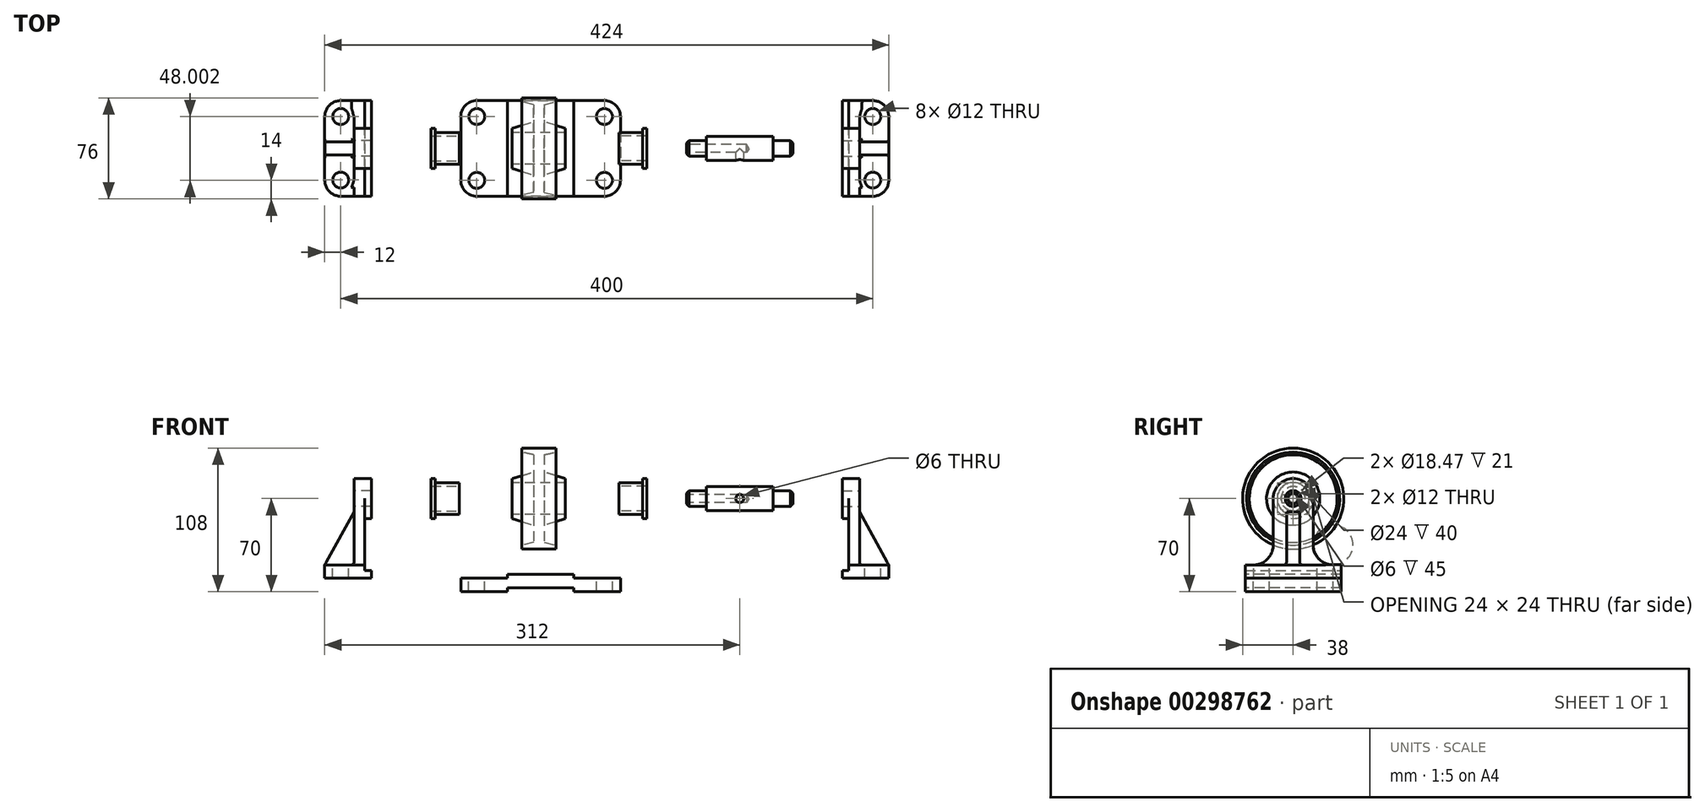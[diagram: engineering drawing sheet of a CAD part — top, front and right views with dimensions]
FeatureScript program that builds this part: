
annotation { "Feature Type Name" : "Feature", "Feature Type Description" : "" }
export const myFeature = defineFeature(function(context is Context, id is Id, definition is map)
    precondition{}
    {
        {
            var Q0;
            Q0=qCreatedBy(makeId("Front.planeOp"),FACE);
            var sketch = newSketch(context, id + "F0", { "sketchPlane" : qUnion([Q0])});
            skLineSegment(sketch, "E0", {"start": v(-300.95, 0) * mm, "end": v(299.05, 0) * mm});
            skSolve(sketch);
        }
        {
            var Q0;
            Q0=qCreatedBy(makeId("Front.planeOp"),FACE);
            var sketch = newSketch(context, id + "F1", { "sketchPlane" : qUnion([Q0])});
            skLineSegment(sketch, "E1", {"start": v(0, 12) * mm, "end": v(20, 12) * mm});
            skLineSegment(sketch, "E2", {"start": v(20, 12) * mm, "end": v(20, 15) * mm});
            skLineSegment(sketch, "E3", {"start": v(20, 15) * mm, "end": v(4, 20) * mm});
            skLineSegment(sketch, "E4", {"start": v(4, 20) * mm, "end": v(4, 33) * mm});
            skLineSegment(sketch, "E5", {"start": v(4, 33) * mm, "end": v(13, 35) * mm});
            skLineSegment(sketch, "E6", {"start": v(13, 35) * mm, "end": v(13, 38) * mm});
            skLineSegment(sketch, "E7", {"start": v(13, 38) * mm, "end": v(0, 38) * mm});
            skLineSegment(sketch, "E8.MirrorCS", {"start": v(-13, 35) * mm, "end": v(-13, 38) * mm});
            skLineSegment(sketch, "E9.MirrorCS", {"start": v(-20, 12) * mm, "end": v(-20, 15) * mm});
            skLineSegment(sketch, "E10.MirrorCS", {"start": v(-13, 38) * mm, "end": v(0, 38) * mm});
            skLineSegment(sketch, "E11.MirrorCS", {"start": v(-4, 33) * mm, "end": v(-13, 35) * mm});
            skLineSegment(sketch, "E12.MirrorCS", {"start": v(-4, 20) * mm, "end": v(-4, 33) * mm});
            skLineSegment(sketch, "E13.MirrorCS", {"start": v(-20, 15) * mm, "end": v(-4, 20) * mm});
            skLineSegment(sketch, "E14.MirrorCS", {"start": v(0, 12) * mm, "end": v(-20, 12) * mm});
            skSolve(sketch);
        }
        {
            var Q0;
            Q0 = qSketchRegion(id + "F1", true);
            var Q1;
            Q1=sQuery(id+"F0.wireOp",EDGE,"E0");
            revolve(context, id + "F2", {"entities" : qUnion([Q0]), "axis" : qUnion([Q1]), "revolveType" : RevolveType.FULL});
        }
        {
            var Q0;
            Q0=qCreatedBy(makeId("Right.planeOp"),FACE);
            cPlane(context, id + "F3", {"entities" : qUnion([Q0]), "cplaneType" : CPlaneType.OFFSET, "offset" : 60 * mm, "oppositeDirection" : true, "width" : 150 * mm, "height" : 150 * mm});
        }
        {
            var Q0;
            Q0=qCreatedBy(id+"F3.planeOp",FACE);
            var sketch = newSketch(context, id + "F4", { "sketchPlane" : qUnion([Q0])});
            skCircle(sketch, "E15.0", {"center": v(0, 0) * mm, "radius": 12 * mm});
            skCircle(sketch, "E16", {"center": v(0, 0) * mm, "radius": 9.24 * mm});
            skSolve(sketch);
        }
        {
            var Q0;
            Q0 = qSketchRegion(id + "F4", true);
            extrude(context, id + "F5", {"entities" : qUnion([Q0]), "oppositeDirection" : true, "depth" : 21 * mm});
        }
        {
            var Q0;
            Q0=makeQuery(id+"F5.opExtrude","CAP_FACE",FACE,{"disambiguationData":[OSD([sQuery(id+"F4.wireOp",EDGE,"E15.0"),sQuery(id+"F4.wireOp",EDGE,"E16")])],"isStart":false});
            var sketch = newSketch(context, id + "F6", { "sketchPlane" : qUnion([Q0])});
            skCircle(sketch, "E17.0", {"center": v(0, 0) * mm, "radius": 9.24 * mm});
            skCircle(sketch, "E18", {"center": v(0, 0) * mm, "radius": 15 * mm});
            skSolve(sketch);
        }
        {
            var Q0;
            Q0 = qSketchRegion(id + "F6", true);
            extrude(context, id + "F7", {"entities" : qUnion([Q0]), "operationType" : NewBodyOperationType.ADD, "oppositeDirection" : true, "depth" : 3 * mm});
        }
        {
            var Q0;
            Q0=makeQuery(id+"F5.opExtrude","SWEPT_BODY",BODY,{"disambiguationData":[OSD([sQuery(id+"F4.wireOp",EDGE,"E15.0"),sQuery(id+"F4.wireOp",EDGE,"E16")])]});
            var Q1;
            Q1=qCreatedBy(makeId("Right.planeOp"),FACE);
            mirror(context, id + "F8", {"entities" : qUnion([Q0]), "mirrorPlane" : qUnion([Q1])});
        }
        {
            var Q0;
            Q0=makeQuery(id+"F8.opPattern","COPY",FACE,{"derivedFrom":makeQuery(id+"F7.boolean.opBoolean","MERGE",FACE,{"derivedFrom":[makeQuery(id+"F5.opExtrude","CAP_FACE",FACE,{"disambiguationData":[OSD([sQuery(id+"F4.wireOp",EDGE,"E15.0"),sQuery(id+"F4.wireOp",EDGE,"E16")])],"isStart":false}),makeQuery(id+"F7.opExtrude","CAP_FACE",FACE,{"disambiguationData":[OSD([sQuery(id+"F6.wireOp",EDGE,"E17.0"),sQuery(id+"F6.wireOp",EDGE,"E18")])],"isStart":true})]}),"instanceName":"1"});
            cPlane(context, id + "F9", {"entities" : qUnion([Q0]), "cplaneType" : CPlaneType.OFFSET, "offset" : 60 * mm, "width" : 150 * mm, "height" : 150 * mm});
        }
        {
            var Q0;
            Q0=qCreatedBy(id+"F9.planeOp",FACE);
            var sketch = newSketch(context, id + "F10", { "sketchPlane" : qUnion([Q0])});
            skCircle(sketch, "E19", {"center": v(0, 0) * mm, "radius": 6 * mm});
            skLineSegment(sketch, "E20", {"start": v(0, 10.72) * mm, "end": v(0, -9.05) * mm, "construction": true});
            skLineSegment(sketch, "E21", {"start": v(11.8, 0) * mm, "end": v(-12.55, 0) * mm, "construction": true});
            skSolve(sketch);
        }
        {
            var Q0;
            Q0 = qSketchRegion(id + "F10", true);
            extrude(context, id + "F11", {"entities" : qUnion([Q0]), "depth" : 80 * mm});
        }
        {
            var Q0;
            Q0=makeQuery(id+"F11.opExtrude","SWEPT_FACE",FACE,{"disambiguationData":[OSD([sQuery(id+"F10.wireOp",EDGE,"E19")])]});
            var Q1;
            Q1=makeQuery(id+"F11.opExtrude","CAP_FACE",FACE,{"disambiguationData":[OSD([sQuery(id+"F10.wireOp",EDGE,"E19")])],"isStart":true});
            chamfer(context, id + "F12", {"entities" : qUnion([Q0, Q1]), "width" : 2 * mm, "tangentPropagation" : true});
        }
        {
            var Q0;
            Q0=qCreatedBy(id+"F9.planeOp",FACE);
            cPlane(context, id + "F13", {"entities" : qUnion([Q0]), "cplaneType" : CPlaneType.OFFSET, "offset" : 15 * mm, "width" : 150 * mm, "height" : 150 * mm});
        }
        {
            var Q0;
            Q0=qCreatedBy(id+"F13.planeOp",FACE);
            var sketch = newSketch(context, id + "F14", { "sketchPlane" : qUnion([Q0])});
            skCircle(sketch, "E22", {"center": v(0, 0) * mm, "radius": 9 * mm});
            skSolve(sketch);
        }
        {
            var Q0;
            Q0 = qSketchRegion(id + "F14", true);
            extrude(context, id + "F15", {"entities" : qUnion([Q0]), "operationType" : NewBodyOperationType.ADD, "depth" : 50 * mm});
        }
        {
            var Q0;
            Q0=makeQuery(id+"F11.opExtrude","SWEPT_BODY",BODY,{"disambiguationData":[OSD([sQuery(id+"F10.wireOp",EDGE,"E19")])]});
            transform(context, id + "F16", {"entities" : qUnion([Q0]), "transformType" : TransformType.TRANSLATION_3D, "dx" : -20 * mm, "dy" : 0 * mm, "dz" : 0 * mm, "makeCopy" : false});
        }
        {
            var Q0;
            Q0=makeQuery(id+"F11.opExtrude","SWEPT_BODY",BODY,{"disambiguationData":[OSD([sQuery(id+"F10.wireOp",EDGE,"E19")])]});
            transform(context, id + "F17", {"entities" : qUnion([Q0]), "transformType" : TransformType.TRANSLATION_3D, "dx" : -10 * mm, "dy" : 0 * mm, "dz" : 0 * mm, "makeCopy" : false});
        }
        {
            var Q0;
            Q0=makeQuery(id+"F11.opExtrude","CAP_FACE",FACE,{"disambiguationData":[OSD([sQuery(id+"F10.wireOp",EDGE,"E19")])],"isStart":true});
            var sketch = newSketch(context, id + "F18", { "sketchPlane" : qUnion([Q0])});
            skCircle(sketch, "E23.0", {"center": v(0, 0) * mm, "radius": 4 * mm});
            skSolve(sketch);
        }
        {
            var Q0;
            Q0=sQuery(id+"F18.wireOp",VERTEX,"E23.0.center");
            var Q1;
            Q1=makeQuery(id+"F11.opExtrude","SWEPT_BODY",BODY,{"disambiguationData":[OSD([sQuery(id+"F10.wireOp",EDGE,"E19")])]});
            hole(context, id + "F19", {"style" : HoleStyle.SIMPLE, "endStyle" : HoleEndStyle.BLIND, "holeDiameter" : 6 * mm, "holeDepth" : 45 * mm, "tappedDepth" : 12 * mm, "tapClearance" : 3, "startFromSketch" : true, "locations" : qUnion([Q0]), "scope" : qUnion([Q1])});
        }
        {
            var Q0;
            Q0=qCreatedBy(makeId("Front.planeOp"),FACE);
            var sketch = newSketch(context, id + "F20", { "sketchPlane" : qUnion([Q0])});
            skCircle(sketch, "E24", {"center": v(151, 0) * mm, "radius": 3 * mm});
            skSolve(sketch);
        }
        {
            var Q0;
            Q0 = qSketchRegion(id + "F20", true);
            extrude(context, id + "F21", {"entities" : qUnion([Q0]), "operationType" : NewBodyOperationType.REMOVE, "depth" : 25 * mm});
        }
        {
            var Q0;
            Q0=makeQuery(id+"F7.boolean.opBoolean","MERGE",FACE,{"derivedFrom":[makeQuery(id+"F5.opExtrude","CAP_FACE",FACE,{"disambiguationData":[OSD([sQuery(id+"F4.wireOp",EDGE,"E15.0"),sQuery(id+"F4.wireOp",EDGE,"E16")])],"isStart":false}),makeQuery(id+"F7.opExtrude","CAP_FACE",FACE,{"disambiguationData":[OSD([sQuery(id+"F6.wireOp",EDGE,"E17.0"),sQuery(id+"F6.wireOp",EDGE,"E18")])],"isStart":true})]});
            cPlane(context, id + "F22", {"entities" : qUnion([Q0]), "cplaneType" : CPlaneType.OFFSET, "offset" : 100 * mm, "width" : 150 * mm, "height" : 150 * mm});
        }
        {
            var Q0;
            Q0=qCreatedBy(id+"F22.planeOp",FACE);
            var sketch = newSketch(context, id + "F23", { "sketchPlane" : qUnion([Q0])});
            skCircle(sketch, "E25.0", {"center": v(0, 0) * mm, "radius": 6 * mm});
            skCircle(sketch, "E26", {"center": v(0, 0) * mm, "radius": 15 * mm});
            skLineSegment(sketch, "E27", {"start": v(-15, 0) * mm, "end": v(-15, -49.82) * mm});
            skLineSegment(sketch, "E28", {"start": v(-15, -49.82) * mm, "end": v(-36, -49.82) * mm});
            skLineSegment(sketch, "E29", {"start": v(15, 0) * mm, "end": v(15, -50) * mm});
            skLineSegment(sketch, "E30", {"start": v(15, -50) * mm, "end": v(36, -50) * mm});
            skLineSegment(sketch, "E31", {"start": v(36, -50) * mm, "end": v(36, -60) * mm});
            skLineSegment(sketch, "E32", {"start": v(36, -60) * mm, "end": v(-36, -60) * mm});
            skLineSegment(sketch, "E33", {"start": v(-36, -60) * mm, "end": v(-36, -49.82) * mm});
            skSolve(sketch);
        }
        {
            var Q0;
            Q0=makeQuery(id+"F23.imprint","IMPRINT",FACE,{"disambiguationData":[TD([[makeQuery(id+"F23.imprint","IMPRINT",EDGE,{"derivedFrom":sQuery(id+"F23.wireOp",EDGE,"E25.0")}),-1.0]])]});
            extrude(context, id + "F24", {"entities" : qUnion([Q0]), "oppositeDirection" : true, "depth" : 5 * mm});
        }
        {
            var Q0;
            Q0=qCreatedBy(id+"F22.planeOp",FACE);
            var sketch = newSketch(context, id + "F25", { "sketchPlane" : qUnion([Q0])});
            skCircle(sketch, "E34.0", {"center": v(0, 0) * mm, "radius": 15 * mm});
            skCircle(sketch, "E35.0", {"center": v(0, 0) * mm, "radius": 6 * mm});
            skLineSegment(sketch, "E36.0", {"start": v(-15, 0) * mm, "end": v(-15, -49.82) * mm});
            skLineSegment(sketch, "E37.0", {"start": v(-15, -49.82) * mm, "end": v(-36, -49.82) * mm});
            skLineSegment(sketch, "E38.0", {"start": v(15, 0) * mm, "end": v(15, -50) * mm});
            skLineSegment(sketch, "E39.0", {"start": v(15, -50) * mm, "end": v(36, -50) * mm});
            skPoint(sketch, "E40.0", {"position": v(36, -55) * mm});
            skLineSegment(sketch, "E41.0", {"start": v(36, -50) * mm, "end": v(36, -60) * mm});
            skLineSegment(sketch, "E42.0", {"start": v(36, -60) * mm, "end": v(-36, -60) * mm});
            skLineSegment(sketch, "E43.0", {"start": v(-36, -60) * mm, "end": v(-36, -49.82) * mm});
            skSolve(sketch);
        }
        {
            var Q0;
            Q0 = qSketchRegion(id + "F25", true);
            extrude(context, id + "F26", {"entities" : qUnion([Q0]), "operationType" : NewBodyOperationType.ADD, "depth" : 8 * mm});
        }
        {
            var Q0;
            Q0=qCreatedBy(id+"F22.planeOp",FACE);
            var sketch = newSketch(context, id + "F27", { "sketchPlane" : qUnion([Q0])});
            skLineSegment(sketch, "E44.0", {"start": v(36, -60) * mm, "end": v(-36, -60) * mm});
            skLineSegment(sketch, "E45", {"start": v(36, -60) * mm, "end": v(36, -54) * mm});
            skLineSegment(sketch, "E46", {"start": v(36, -54) * mm, "end": v(-36, -54) * mm});
            skLineSegment(sketch, "E47", {"start": v(-36, -54) * mm, "end": v(-36, -60) * mm});
            skSolve(sketch);
        }
        {
            var Q0;
            Q0 = qSketchRegion(id + "F27", true);
            extrude(context, id + "F28", {"entities" : qUnion([Q0]), "operationType" : NewBodyOperationType.ADD, "oppositeDirection" : true, "depth" : 5 * mm});
        }
        {
            var Q0;
            Q0=makeQuery(id+"F26.opExtrude","CAP_FACE",FACE,{"disambiguationData":[OSD([sQuery(id+"F25.wireOp",EDGE,"E34.0"),sQuery(id+"F25.wireOp",EDGE,"E35.0"),sQuery(id+"F25.wireOp",EDGE,"E36.0"),sQuery(id+"F25.wireOp",EDGE,"E37.0"),sQuery(id+"F25.wireOp",EDGE,"E38.0"),sQuery(id+"F25.wireOp",EDGE,"E39.0"),sQuery(id+"F25.wireOp",EDGE,"E41.0"),sQuery(id+"F25.wireOp",EDGE,"E42.0"),sQuery(id+"F25.wireOp",EDGE,"E43.0")])],"isStart":false});
            var sketch = newSketch(context, id + "F29", { "sketchPlane" : qUnion([Q0])});
            skLineSegment(sketch, "E48.0", {"start": v(36, -60) * mm, "end": v(-36, -60) * mm});
            skLineSegment(sketch, "E49", {"start": v(-36, -60) * mm, "end": v(-36, -49.82) * mm});
            skLineSegment(sketch, "E50", {"start": v(-36, -49.82) * mm, "end": v(36, -50) * mm});
            skLineSegment(sketch, "E51", {"start": v(36, -50) * mm, "end": v(36, -60) * mm});
            skSolve(sketch);
        }
        {
            var Q0;
            Q0 = qSketchRegion(id + "F29", true);
            extrude(context, id + "F30", {"entities" : qUnion([Q0]), "operationType" : NewBodyOperationType.ADD, "depth" : 22 * mm});
        }
        {
            var Q0;
            Q0=makeQuery(id+"F26.opExtrude","SWEPT_EDGE",EDGE,{"disambiguationData":[OSD([sQuery(id+"F25.wireOp",EDGE,"E38.0"),sQuery(id+"F25.wireOp",EDGE,"E39.0")])]});
            var Q1;
            Q1=makeQuery(id+"F26.opExtrude","SWEPT_EDGE",EDGE,{"disambiguationData":[OSD([sQuery(id+"F25.wireOp",EDGE,"E36.0"),sQuery(id+"F25.wireOp",EDGE,"E37.0")])]});
            fillet(context, id + "F31", {"entities" : qUnion([Q0, Q1]), "radius" : 15 * mm, "tangentPropagation" : true, "allowEdgeOverflow" : false});
        }
        {
            var Q0;
            Q0=makeQuery(id+"F30.opExtrude","CAP_EDGE",EDGE,{"disambiguationData":[OSD([sQuery(id+"F29.wireOp",EDGE,"E51")])],"isStart":false});
            var Q1;
            Q1=makeQuery(id+"F30.opExtrude","CAP_EDGE",EDGE,{"disambiguationData":[OSD([sQuery(id+"F29.wireOp",EDGE,"E49")])],"isStart":false});
            fillet(context, id + "F32", {"entities" : qUnion([Q0, Q1]), "radius" : 12 * mm, "tangentPropagation" : true, "allowEdgeOverflow" : false});
        }
        {
            var Q0;
            Q0=makeQuery(id+"F26.opExtrude","SWEPT_FACE",FACE,{"disambiguationData":[OSD([sQuery(id+"F25.wireOp",EDGE,"E38.0")])]});
            cPlane(context, id + "F33", {"entities" : qUnion([Q0]), "cplaneType" : CPlaneType.OFFSET, "offset" : 15 * mm, "oppositeDirection" : true, "width" : 150 * mm, "height" : 150 * mm});
        }
        {
            var Q0;
            Q0=qCreatedBy(id+"F33.planeOp",FACE);
            var sketch = newSketch(context, id + "F34", { "sketchPlane" : qUnion([Q0])});
            skLineSegment(sketch, "E52", {"start": v(-189, -49.98) * mm, "end": v(-211, -49.98) * mm});
            skLineSegment(sketch, "E53", {"start": v(-189, -49.98) * mm, "end": v(-189, -9.98) * mm});
            skLineSegment(sketch, "E54", {"start": v(-189, -9.98) * mm, "end": v(-211, -49.98) * mm});
            skSolve(sketch);
        }
        {
            var Q0;
            Q0 = qSketchRegion(id + "F34", true);
            extrude(context, id + "F35", {"entities" : qUnion([Q0]), "operationType" : NewBodyOperationType.ADD, "endBound" : BoundingType.SYMMETRIC, "depth" : 10 * mm});
        }
        {
            var Q0;
            Q0=makeQuery(id+"F35.boolean.opBoolean","INTERSECT",EDGE,{"derivedFrom":[makeQuery(id+"F30.opExtrude","SWEPT_FACE",FACE,{"disambiguationData":[OSD([sQuery(id+"F29.wireOp",EDGE,"E50")])]}),makeQuery(id+"F35.opExtrude","CAP_FACE",FACE,{"disambiguationData":[OSD([sQuery(id+"F34.wireOp",EDGE,"E52"),sQuery(id+"F34.wireOp",EDGE,"E53"),sQuery(id+"F34.wireOp",EDGE,"E54")])],"isStart":false})]});
            var Q1;
            {var subQ0=sQuery(id+"F25.wireOp",EDGE,"E39.0");var subQ1=sQuery(id+"F25.wireOp",EDGE,"E38.0");var subQ2=sQuery(id+"F29.wireOp",EDGE,"E50");var subQ3=makeQuery(id+"F30.opExtrude","CAP_FACE",FACE,{"disambiguationData":[OSD([sQuery(id+"F29.wireOp",EDGE,"E48.0"),sQuery(id+"F29.wireOp",EDGE,"E49"),subQ2,sQuery(id+"F29.wireOp",EDGE,"E51")])],"isStart":true});var subQ5=makeQuery(id+"F26.opExtrude","CAP_FACE",FACE,{"disambiguationData":[OSD([sQuery(id+"F25.wireOp",EDGE,"E34.0"),sQuery(id+"F25.wireOp",EDGE,"E35.0"),sQuery(id+"F25.wireOp",EDGE,"E36.0"),sQuery(id+"F25.wireOp",EDGE,"E37.0"),subQ1,subQ0,sQuery(id+"F25.wireOp",EDGE,"E41.0"),sQuery(id+"F25.wireOp",EDGE,"E42.0"),sQuery(id+"F25.wireOp",EDGE,"E43.0")])],"isStart":false});var subQ6=makeQuery(id+"F30.opExtrude","CAP_EDGE",EDGE,{"disambiguationData":[OSD([subQ2])],"isStart":true});Q1=makeQuery(id+"F35.boolean.opBoolean","SPLIT",EDGE,{"disambiguationData":[TD([makeQuery(id+"F31.opFillet","BLEND_FACE",FACE,{"disambiguationData":[OSD([subQ1,subQ0])]})])],"derivedFrom":makeQuery(id+"F31.opFillet","MERGE",EDGE,{"derivedFrom":[makeQuery(id+"F30.boolean.opBoolean","SPLIT",EDGE,{"disambiguationData":[topologyDisambiguationEdgeConnected([subQ5])],"derivedFrom":subQ6}),makeQuery(id+"F30.boolean.opBoolean","SPLIT",EDGE,{"disambiguationData":[topologyDisambiguationEdgeConnected([subQ3])],"derivedFrom":subQ6})]})});}
            var Q2;
            Q2=makeQuery(id+"F35.opExtrude","CAP_EDGE",EDGE,{"disambiguationData":[OSD([sQuery(id+"F34.wireOp",EDGE,"E53")])],"isStart":false});
            var Q3;
            {var subQ0=sQuery(id+"F25.wireOp",EDGE,"E43.0");var subQ1=sQuery(id+"F25.wireOp",EDGE,"E37.0");var subQ2=makeQuery(id+"F26.opExtrude","CAP_FACE",FACE,{"disambiguationData":[OSD([sQuery(id+"F25.wireOp",EDGE,"E34.0"),sQuery(id+"F25.wireOp",EDGE,"E35.0"),sQuery(id+"F25.wireOp",EDGE,"E36.0"),subQ1,sQuery(id+"F25.wireOp",EDGE,"E38.0"),sQuery(id+"F25.wireOp",EDGE,"E39.0"),sQuery(id+"F25.wireOp",EDGE,"E41.0"),sQuery(id+"F25.wireOp",EDGE,"E42.0"),subQ0])],"isStart":false});var subQ3=sQuery(id+"F29.wireOp",EDGE,"E49");var subQ4=sQuery(id+"F29.wireOp",EDGE,"E50");var subQ6=makeQuery(id+"F30.opExtrude","CAP_EDGE",EDGE,{"disambiguationData":[OSD([subQ4])],"isStart":true});Q3=makeQuery(id+"F35.boolean.opBoolean","SPLIT",EDGE,{"disambiguationData":[TD([makeQuery(id+"F26.opExtrude","SWEPT_FACE",FACE,{"disambiguationData":[OSD([subQ1])]})])],"derivedFrom":makeQuery(id+"F31.opFillet","MERGE",EDGE,{"derivedFrom":[makeQuery(id+"F30.boolean.opBoolean","SPLIT",EDGE,{"disambiguationData":[topologyDisambiguationEdgeConnected([subQ2])],"derivedFrom":subQ6}),makeQuery(id+"F30.boolean.opBoolean","SPLIT",EDGE,{"disambiguationData":[topologyDisambiguationEdgeConnected([makeQuery(id+"F30.opExtrude","CAP_FACE",FACE,{"disambiguationData":[OSD([sQuery(id+"F29.wireOp",EDGE,"E48.0"),subQ3,subQ4,sQuery(id+"F29.wireOp",EDGE,"E51")])],"isStart":true})])],"derivedFrom":subQ6})]})});}
            var Q4;
            Q4=makeQuery(id+"F35.opExtrude","CAP_EDGE",EDGE,{"disambiguationData":[OSD([sQuery(id+"F34.wireOp",EDGE,"E53")])],"isStart":true});
            var Q5;
            Q5=makeQuery(id+"F35.boolean.opBoolean","INTERSECT",EDGE,{"derivedFrom":[makeQuery(id+"F30.opExtrude","SWEPT_FACE",FACE,{"disambiguationData":[OSD([sQuery(id+"F29.wireOp",EDGE,"E50")])]}),makeQuery(id+"F35.opExtrude","CAP_FACE",FACE,{"disambiguationData":[OSD([sQuery(id+"F34.wireOp",EDGE,"E52"),sQuery(id+"F34.wireOp",EDGE,"E53"),sQuery(id+"F34.wireOp",EDGE,"E54")])],"isStart":true})]});
            var Q6;
            Q6=makeQuery(id+"F24.opExtrude","CAP_EDGE",EDGE,{"disambiguationData":[OSD([sQuery(id+"F23.wireOp",EDGE,"E26")])],"isStart":true});
            fillet(context, id + "F36", {"entities" : qUnion([Q0, Q1, Q2, Q3, Q4, Q5, Q6]), "radius" : 2 * mm, "tangentPropagation" : true, "allowEdgeOverflow" : false});
        }
        {
            var Q0;
            Q0=makeQuery(id+"F30.opExtrude","SWEPT_FACE",FACE,{"disambiguationData":[OSD([sQuery(id+"F29.wireOp",EDGE,"E50")])]});
            var sketch = newSketch(context, id + "F37", { "sketchPlane" : qUnion([Q0])});
            skCircle(sketch, "E55", {"center": v(-199, 23.88) * mm, "radius": 6 * mm});
            skCircle(sketch, "E56.MirrorC", {"center": v(-199, -23.88) * mm, "radius": 6 * mm});
            skSolve(sketch);
        }
        {
            var Q0;
            Q0 = qSketchRegion(id + "F37", true);
            extrude(context, id + "F38", {"entities" : qUnion([Q0]), "operationType" : NewBodyOperationType.REMOVE, "endBound" : BoundingType.THROUGH_ALL, "oppositeDirection" : true, "depth" : 10 * mm});
        }
        {
            var Q0;
            Q0=makeQuery(id+"F24.opExtrude","SWEPT_BODY",BODY,{"disambiguationData":[OSD([sQuery(id+"F23.wireOp",EDGE,"E25.0"),sQuery(id+"F23.wireOp",EDGE,"E26")])]});
            var Q1;
            Q1=qCreatedBy(id+"F9.planeOp",FACE);
            mirror(context, id + "F39", {"entities" : qUnion([Q0]), "mirrorPlane" : qUnion([Q1])});
        }
        {
            var Q0;
            Q0=makeQuery(id+"F39.opPattern","COPY",BODY,{"derivedFrom":makeQuery(id+"F24.opExtrude","SWEPT_BODY",BODY,{"disambiguationData":[OSD([sQuery(id+"F23.wireOp",EDGE,"E25.0"),sQuery(id+"F23.wireOp",EDGE,"E26")])]}),"instanceName":"1"});
            transform(context, id + "F40", {"entities" : qUnion([Q0]), "transformType" : TransformType.TRANSLATION_3D, "dx" : -230 * mm, "dy" : 0 * mm, "dz" : 0 * mm, "makeCopy" : false});
        }
        {
            var Q0;
            Q0=makeQuery(id+"F24.opExtrude","SWEPT_BODY",BODY,{"disambiguationData":[OSD([sQuery(id+"F23.wireOp",EDGE,"E25.0"),sQuery(id+"F23.wireOp",EDGE,"E26")])]});
            transform(context, id + "F41", {"entities" : qUnion([Q0]), "transformType" : TransformType.TRANSLATION_3D, "dx" : 50 * mm, "dy" : 0 * mm, "dz" : 0 * mm, "makeCopy" : false});
        }
        {
            var Q0;
            Q0=qCreatedBy(makeId("Front.planeOp"),FACE);
            cPlane(context, id + "F42", {"entities" : qUnion([Q0]), "cplaneType" : CPlaneType.OFFSET, "offset" : 36 * mm, "width" : 150 * mm, "height" : 150 * mm});
        }
        {
            var Q0;
            Q0=qCreatedBy(id+"F42.planeOp",FACE);
            var sketch = newSketch(context, id + "F43", { "sketchPlane" : qUnion([Q0])});
            skLineSegment(sketch, "E57.0", {"start": v(-300.95, 0) * mm, "end": v(299.05, 0) * mm});
            skLineSegment(sketch, "E58", {"start": v(-73.71, -60) * mm, "end": v(-38.71, -60) * mm});
            skLineSegment(sketch, "E59", {"start": v(-38.71, -60) * mm, "end": v(-38.71, -57) * mm});
            skLineSegment(sketch, "E60", {"start": v(-38.71, -57) * mm, "end": v(11.29, -57) * mm});
            skLineSegment(sketch, "E61", {"start": v(11.29, -57) * mm, "end": v(11.29, -60) * mm});
            skLineSegment(sketch, "E62", {"start": v(11.29, -60) * mm, "end": v(46.29, -60) * mm});
            skLineSegment(sketch, "E63", {"start": v(46.29, -60) * mm, "end": v(46.29, -50) * mm});
            skLineSegment(sketch, "E64", {"start": v(46.29, -50) * mm, "end": v(11.29, -50) * mm});
            skLineSegment(sketch, "E65", {"start": v(11.29, -50) * mm, "end": v(11.29, -47) * mm});
            skLineSegment(sketch, "E66", {"start": v(11.29, -47) * mm, "end": v(-38.71, -47) * mm});
            skLineSegment(sketch, "E67", {"start": v(-38.71, -47) * mm, "end": v(-38.71, -50) * mm});
            skLineSegment(sketch, "E68", {"start": v(-38.71, -50) * mm, "end": v(-73.71, -50) * mm});
            skLineSegment(sketch, "E69", {"start": v(-73.71, -50) * mm, "end": v(-73.71, -60) * mm});
            skSolve(sketch);
        }
        {
            var Q0;
            Q0 = qSketchRegion(id + "F43", true);
            extrude(context, id + "F44", {"entities" : qUnion([Q0]), "oppositeDirection" : true, "depth" : 72 * mm});
        }
        {
            var Q0;
            Q0=makeQuery(id+"F44.opExtrude","SWEPT_BODY",BODY,{"disambiguationData":[OSD([sQuery(id+"F43.wireOp",EDGE,"E58"),sQuery(id+"F43.wireOp",EDGE,"E59"),sQuery(id+"F43.wireOp",EDGE,"E60"),sQuery(id+"F43.wireOp",EDGE,"E61"),sQuery(id+"F43.wireOp",EDGE,"E62"),sQuery(id+"F43.wireOp",EDGE,"E63"),sQuery(id+"F43.wireOp",EDGE,"E64"),sQuery(id+"F43.wireOp",EDGE,"E65"),sQuery(id+"F43.wireOp",EDGE,"E66"),sQuery(id+"F43.wireOp",EDGE,"E67"),sQuery(id+"F43.wireOp",EDGE,"E68"),sQuery(id+"F43.wireOp",EDGE,"E69")])]});
            transform(context, id + "F45", {"entities" : qUnion([Q0]), "transformType" : TransformType.TRANSLATION_3D, "dx" : 15 * mm, "dy" : -10 * mm, "dz" : 0 * mm, "makeCopy" : false});
        }
        {
            var Q0;
            Q0=makeQuery(id+"F44.opExtrude","SWEPT_BODY",BODY,{"disambiguationData":[OSD([sQuery(id+"F43.wireOp",EDGE,"E58"),sQuery(id+"F43.wireOp",EDGE,"E59"),sQuery(id+"F43.wireOp",EDGE,"E60"),sQuery(id+"F43.wireOp",EDGE,"E61"),sQuery(id+"F43.wireOp",EDGE,"E62"),sQuery(id+"F43.wireOp",EDGE,"E63"),sQuery(id+"F43.wireOp",EDGE,"E64"),sQuery(id+"F43.wireOp",EDGE,"E65"),sQuery(id+"F43.wireOp",EDGE,"E66"),sQuery(id+"F43.wireOp",EDGE,"E67"),sQuery(id+"F43.wireOp",EDGE,"E68"),sQuery(id+"F43.wireOp",EDGE,"E69")])]});
            transform(context, id + "F46", {"entities" : qUnion([Q0]), "transformType" : TransformType.TRANSLATION_3D, "dx" : 0 * mm, "dy" : 10 * mm, "dz" : -10 * mm, "makeCopy" : false});
        }
        {
            var Q0;
            Q0=makeQuery(id+"F44.opExtrude","CAP_EDGE",EDGE,{"disambiguationData":[OSD([sQuery(id+"F43.wireOp",EDGE,"E69")])],"isStart":true});
            var Q1;
            Q1=makeQuery(id+"F44.opExtrude","CAP_EDGE",EDGE,{"disambiguationData":[OSD([sQuery(id+"F43.wireOp",EDGE,"E63")])],"isStart":true});
            var Q2;
            Q2=makeQuery(id+"F44.opExtrude","CAP_EDGE",EDGE,{"disambiguationData":[OSD([sQuery(id+"F43.wireOp",EDGE,"E63")])],"isStart":false});
            var Q3;
            Q3=makeQuery(id+"F44.opExtrude","CAP_EDGE",EDGE,{"disambiguationData":[OSD([sQuery(id+"F43.wireOp",EDGE,"E69")])],"isStart":false});
            fillet(context, id + "F47", {"entities" : qUnion([Q0, Q1, Q2, Q3]), "radius" : 12 * mm, "tangentPropagation" : true, "allowEdgeOverflow" : false});
        }
        {
            var Q0;
            Q0=makeQuery(id+"F44.opExtrude","SWEPT_FACE",FACE,{"disambiguationData":[OSD([sQuery(id+"F43.wireOp",EDGE,"E64")])]});
            var sketch = newSketch(context, id + "F48", { "sketchPlane" : qUnion([Q0])});
            skLineSegment(sketch, "E70.0", {"start": v(-300.95, 0) * mm, "end": v(299.05, 0) * mm});
            skCircle(sketch, "E71", {"center": v(49.29, 24) * mm, "radius": 6 * mm});
            skCircle(sketch, "E72.MirrorC", {"center": v(49.29, -24) * mm, "radius": 6 * mm});
            skCircle(sketch, "E73", {"center": v(-46.71, 24) * mm, "radius": 6 * mm});
            skCircle(sketch, "E74.MirrorC", {"center": v(-46.71, -24) * mm, "radius": 6 * mm});
            skSolve(sketch);
        }
        {
            var Q0;
            Q0 = qSketchRegion(id + "F48", true);
            var Q1;
            Q1=makeQuery(id+"F44.opExtrude","SWEPT_FACE",FACE,{"disambiguationData":[OSD([sQuery(id+"F43.wireOp",EDGE,"E62")])]});
            extrude(context, id + "F49", {"entities" : qUnion([Q0]), "operationType" : NewBodyOperationType.REMOVE, "endBound" : BoundingType.UP_TO_SURFACE, "oppositeDirection" : true, "endBoundEntityFace" : qUnion([Q1]), "depth" : 25 * mm});
        }
    });
